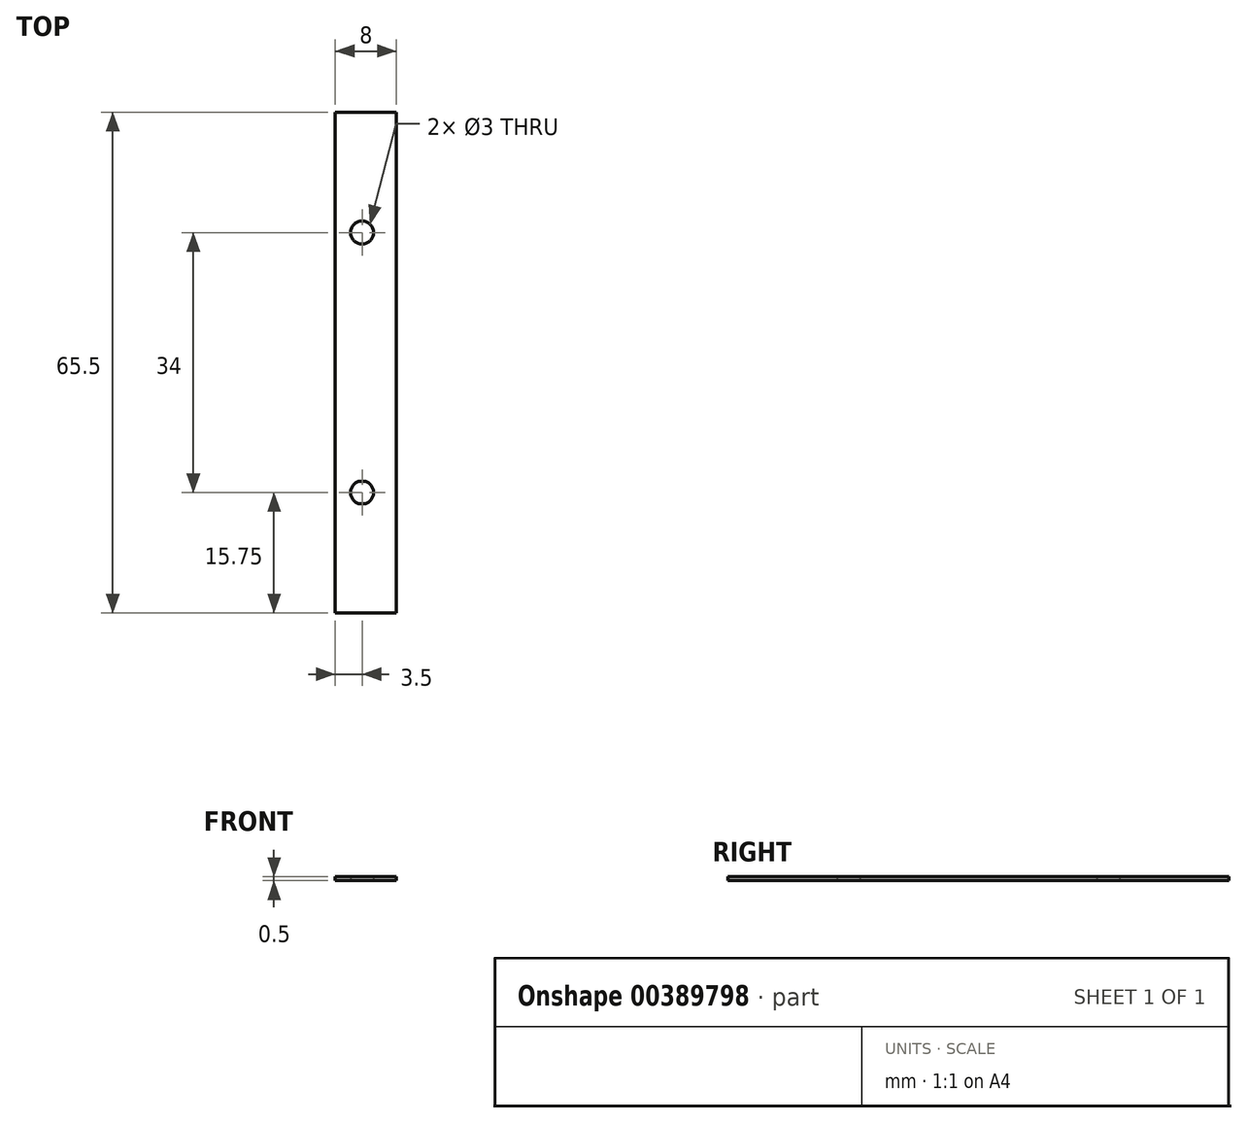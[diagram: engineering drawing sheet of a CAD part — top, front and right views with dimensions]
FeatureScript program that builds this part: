
annotation { "Feature Type Name" : "Feature", "Feature Type Description" : "" }
export const myFeature = defineFeature(function(context is Context, id is Id, definition is map)
    precondition{}
    {
        {
            var Q0;
            Q0=qCreatedBy(makeId("Top.planeOp"),FACE);
            var sketch = newSketch(context, id + "F0", { "sketchPlane" : qUnion([Q0])});
            skLineSegment(sketch, "E0.bottom", {"start": v(-26.98, -42.04) * mm, "end": v(-18.98, -42.04) * mm});
            skLineSegment(sketch, "E0.top", {"start": v(-26.98, 23.46) * mm, "end": v(-18.98, 23.46) * mm});
            skLineSegment(sketch, "E0.left", {"start": v(-26.98, -42.04) * mm, "end": v(-26.98, 23.46) * mm});
            skLineSegment(sketch, "E0.right", {"start": v(-18.98, -42.04) * mm, "end": v(-18.98, 23.46) * mm});
            skPoint(sketch, "E1", {"position": v(-23.48, -26.3) * mm});
            skPoint(sketch, "E2", {"position": v(-23.48, 7.7) * mm});
            skCircle(sketch, "E3", {"center": v(-23.48, -26.3) * mm, "radius": 1.5 * mm});
            skCircle(sketch, "E4", {"center": v(-23.48, 7.7) * mm, "radius": 1.5 * mm});
            skSolve(sketch);
        }
        {
            var Q0;
            Q0 = qSketchRegion(id + "F0", true);
            extrude(context, id + "F1", {"entities" : qUnion([Q0]), "depth" : 0.5 * mm});
        }
    });
